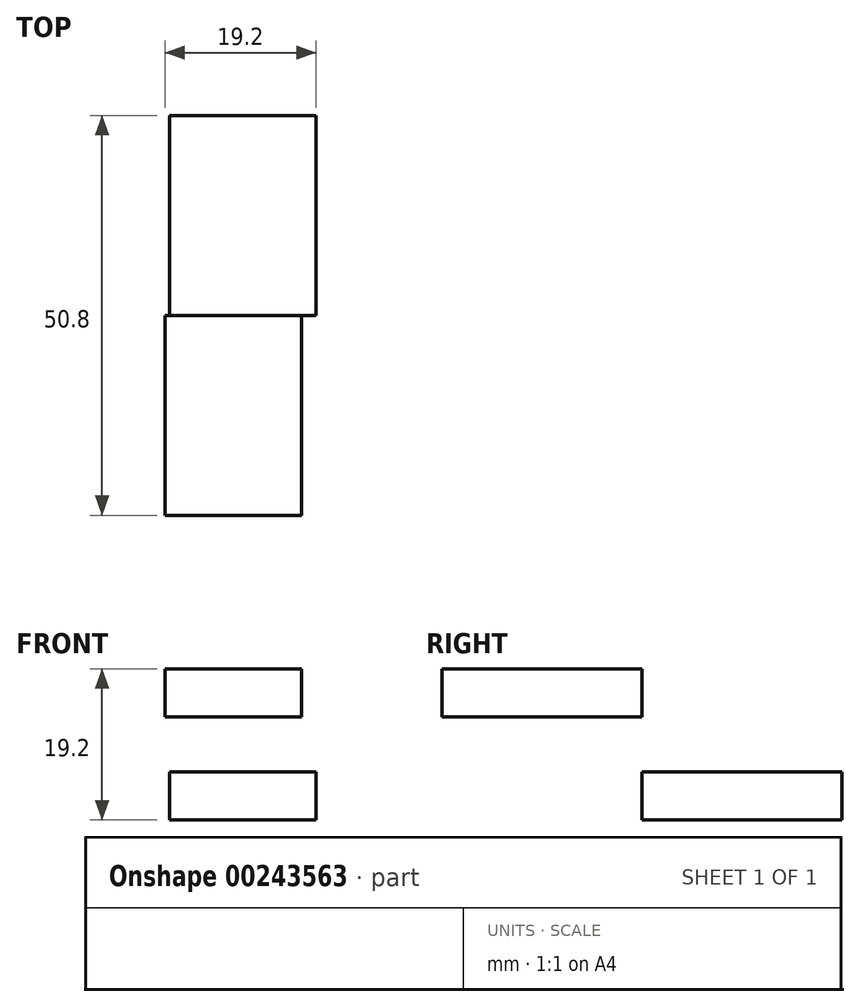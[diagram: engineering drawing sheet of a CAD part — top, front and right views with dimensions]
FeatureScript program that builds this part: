
annotation { "Feature Type Name" : "Feature", "Feature Type Description" : "" }
export const myFeature = defineFeature(function(context is Context, id is Id, definition is map)
    precondition{}
    {
        {
            var Q0;
            Q0=qCreatedBy(makeId("Front.planeOp"),FACE);
            var sketch = newSketch(context, id + "F0", { "sketchPlane" : qUnion([Q0])});
            skLineSegment(sketch, "E0", {"start": v(-62.79, 13.87) * mm, "end": v(-44.2, 13.87) * mm});
            skLineSegment(sketch, "E1", {"start": v(-44.2, 13.87) * mm, "end": v(-44.2, 19.96) * mm});
            skLineSegment(sketch, "E2", {"start": v(-44.2, 19.96) * mm, "end": v(-62.79, 19.96) * mm});
            skLineSegment(sketch, "E3", {"start": v(-62.79, 19.96) * mm, "end": v(-62.79, 13.87) * mm});
            skLineSegment(sketch, "E4", {"start": v(-63.4, 30.02) * mm, "end": v(-44.2, 30.02) * mm});
            skLineSegment(sketch, "E5", {"start": v(-44.2, 30.02) * mm, "end": v(-44.2, 36.12) * mm});
            skLineSegment(sketch, "E6", {"start": v(-44.2, 36.12) * mm, "end": v(-62.79, 36.12) * mm});
            skLineSegment(sketch, "E7", {"start": v(-63.4, 30.02) * mm, "end": v(-63.4, 36.12) * mm});
            skSolve(sketch);
        }
        {
            var Q0;
            Q0=makeQuery(id+"F0.imprint","IMPRINT",FACE,{"disambiguationData":[TD([[makeQuery(id+"F0.imprint","IMPRINT",EDGE,{"derivedFrom":sQuery(id+"F0.wireOp",EDGE,"E0")}),1.0]])]});
            extrude(context, id + "F1", {"entities" : qUnion([Q0]), "depth" : 25.4 * mm});
        }
        {
            var Q0;
            Q0=makeQuery(id+"F1.opExtrude","CAP_FACE",FACE,{"disambiguationData":[OSD([sQuery(id+"F0.wireOp",EDGE,"E0"),sQuery(id+"F0.wireOp",EDGE,"E1"),sQuery(id+"F0.wireOp",EDGE,"E2"),sQuery(id+"F0.wireOp",EDGE,"E3")])],"isStart":false});
            var sketch = newSketch(context, id + "F2", { "sketchPlane" : qUnion([Q0])});
            skLineSegment(sketch, "E8", {"start": v(-63.4, 33.07) * mm, "end": v(-46.02, 33.07) * mm});
            skLineSegment(sketch, "E9", {"start": v(-46.02, 33.07) * mm, "end": v(-46.02, 26.97) * mm});
            skLineSegment(sketch, "E10", {"start": v(-46.02, 26.97) * mm, "end": v(-63.4, 26.97) * mm});
            skLineSegment(sketch, "E11", {"start": v(-63.4, 26.97) * mm, "end": v(-63.4, 33.07) * mm});
            skSolve(sketch);
        }
        {
            var Q0;
            Q0=makeQuery(id+"F2.imprint","IMPRINT",FACE,{"disambiguationData":[TD([[makeQuery(id+"F2.imprint","IMPRINT",EDGE,{"derivedFrom":sQuery(id+"F2.wireOp",EDGE,"E8")}),-1.0]])]});
            extrude(context, id + "F3", {"entities" : qUnion([Q0]), "depth" : 25.4 * mm});
        }
    });
